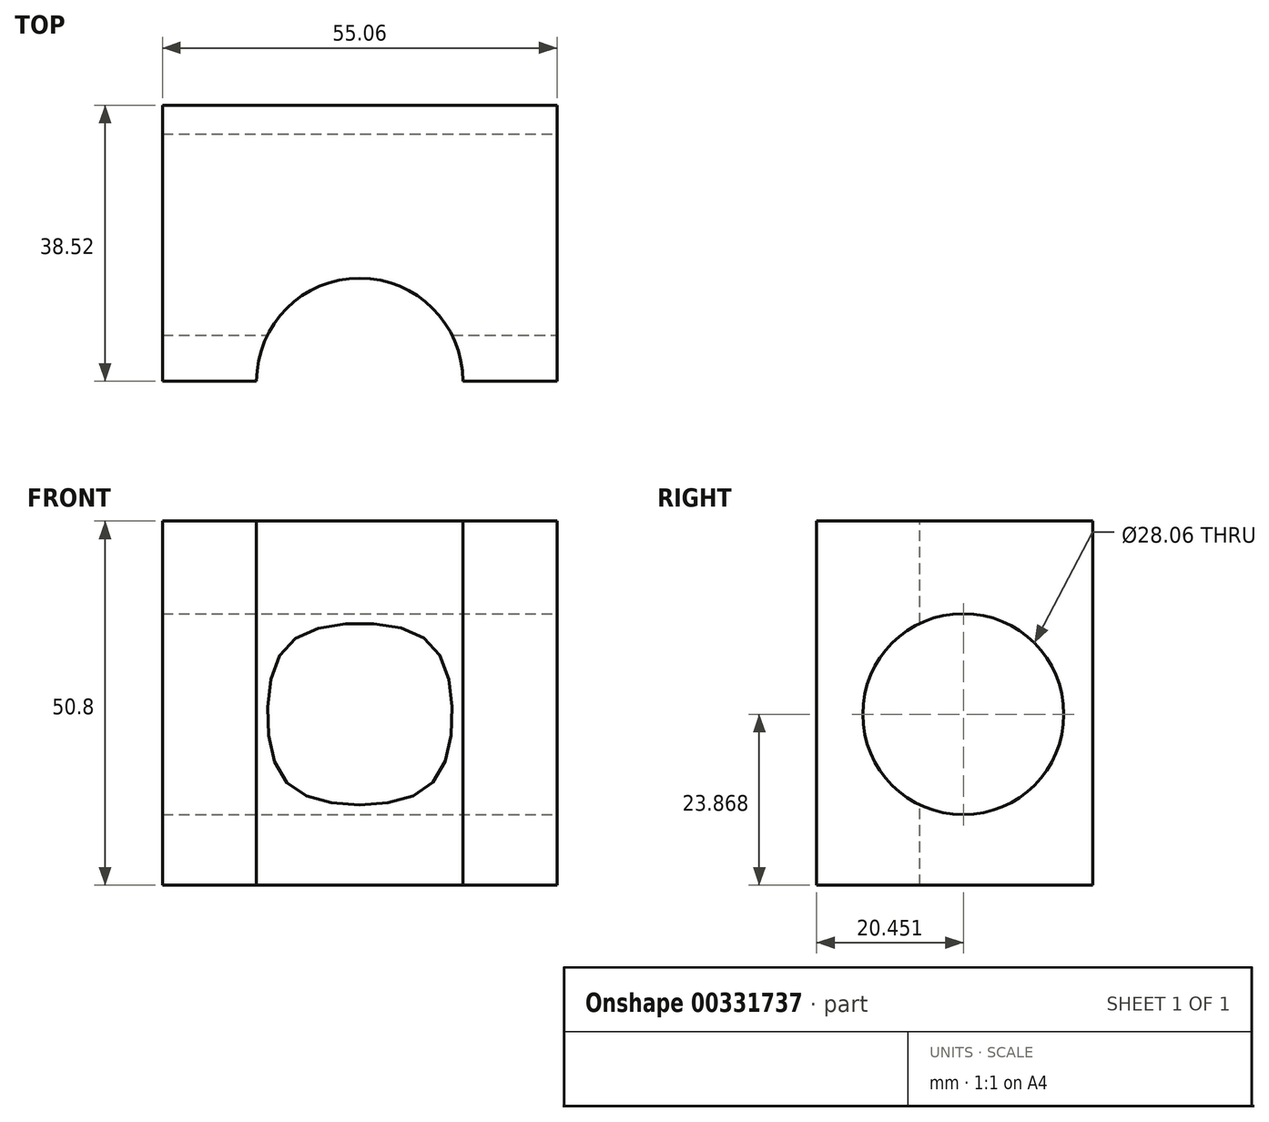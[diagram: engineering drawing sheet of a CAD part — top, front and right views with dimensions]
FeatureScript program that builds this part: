
annotation { "Feature Type Name" : "Feature", "Feature Type Description" : "" }
export const myFeature = defineFeature(function(context is Context, id is Id, definition is map)
    precondition{}
    {
        {
            var Q0;
            Q0=qCreatedBy(makeId("Top.planeOp"),FACE);
            var sketch = newSketch(context, id + "F0", { "sketchPlane" : qUnion([Q0])});
            skLineSegment(sketch, "E0.bottom", {"start": v(0, 0) * mm, "end": v(55.06, 0) * mm});
            skLineSegment(sketch, "E0.top", {"start": v(0, -38.52) * mm, "end": v(55.06, -38.52) * mm});
            skLineSegment(sketch, "E0.left", {"start": v(0, 0) * mm, "end": v(0, -38.52) * mm});
            skLineSegment(sketch, "E0.right", {"start": v(55.06, 0) * mm, "end": v(55.06, -38.52) * mm});
            skSolve(sketch);
        }
        {
            var Q0;
            Q0=makeQuery(id+"F0.imprint","IMPRINT",FACE,{"disambiguationData":[TD([[makeQuery(id+"F0.imprint","IMPRINT",EDGE,{"derivedFrom":sQuery(id+"F0.wireOp",EDGE,"E0.bottom")}),-1.0]])]});
            extrude(context, id + "F1", {"entities" : qUnion([Q0]), "depth" : 50.8 * mm});
        }
        {
            var Q0;
            Q0=makeQuery(id+"F1.opExtrude","CAP_FACE",FACE,{"disambiguationData":[OSD([sQuery(id+"F0.wireOp",EDGE,"E0.bottom"),sQuery(id+"F0.wireOp",EDGE,"E0.top"),sQuery(id+"F0.wireOp",EDGE,"E0.left"),sQuery(id+"F0.wireOp",EDGE,"E0.right")])],"isStart":false});
            var sketch = newSketch(context, id + "F2", { "sketchPlane" : qUnion([Q0])});
            skCircle(sketch, "E1", {"center": v(27.53, -38.52) * mm, "radius": 14.4 * mm});
            skSolve(sketch);
        }
        {
            var Q0;
            {var subQ0=sQuery(id+"F2.wireOp",EDGE,"E1");var subQ1=makeQuery(id+"F1.opExtrude","CAP_EDGE",EDGE,{"disambiguationData":[OSD([sQuery(id+"F0.wireOp",EDGE,"E0.top")])],"isStart":false});var subQ2=makeQuery(id+"F2.imprint","INTERSECT",VERTEX,{"disambiguationData":[OD(0.0)],"derivedFrom":[subQ1,subQ0]});Q0=makeQuery(id+"F2.imprint","IMPRINT",FACE,{"disambiguationData":[TD([[makeQuery(id+"F2.imprint","IMPRINT",EDGE,{"disambiguationData":[TD([[subQ2,-1.0]])],"derivedFrom":subQ0}),1.0]])]});}
            var Q1;
            {var subQ0=sQuery(id+"F2.wireOp",EDGE,"E1");var subQ1=makeQuery(id+"F1.opExtrude","CAP_EDGE",EDGE,{"disambiguationData":[OSD([sQuery(id+"F0.wireOp",EDGE,"E0.top")])],"isStart":false});var subQ2=makeQuery(id+"F2.imprint","INTERSECT",VERTEX,{"disambiguationData":[OD(0.0)],"derivedFrom":[subQ1,subQ0]});Q1=makeQuery(id+"F2.imprint","IMPRINT",FACE,{"disambiguationData":[TD([[makeQuery(id+"F2.imprint","IMPRINT",EDGE,{"disambiguationData":[TD([[subQ2,1.0]])],"derivedFrom":subQ0}),1.0]])]});}
            extrude(context, id + "F3", {"entities" : qUnion([Q0, Q1]), "operationType" : NewBodyOperationType.REMOVE, "oppositeDirection" : true, "depth" : 76.2 * mm});
        }
        {
            var Q0;
            Q0=makeQuery(id+"F1.opExtrude","SWEPT_FACE",FACE,{"disambiguationData":[OSD([sQuery(id+"F0.wireOp",EDGE,"E0.right")])]});
            var sketch = newSketch(context, id + "F4", { "sketchPlane" : qUnion([Q0])});
            skCircle(sketch, "E2", {"center": v(-18.07, 23.87) * mm, "radius": 14.03 * mm});
            skSolve(sketch);
        }
        {
            var Q0;
            Q0=makeQuery(id+"F4.imprint","IMPRINT",FACE,{"disambiguationData":[TD([[makeQuery(id+"F4.imprint","IMPRINT",EDGE,{"derivedFrom":sQuery(id+"F4.wireOp",EDGE,"E2")}),1.0]])]});
            var Q1;
            Q1=sQuery(id+"F4.wireOp",EDGE,"E2");
            extrude(context, id + "F5", {"entities" : qUnion([Q0]), "operationType" : NewBodyOperationType.REMOVE, "surfaceEntities" : qUnion([Q1]), "oppositeDirection" : true, "depth" : 76.2 * mm});
        }
    });
